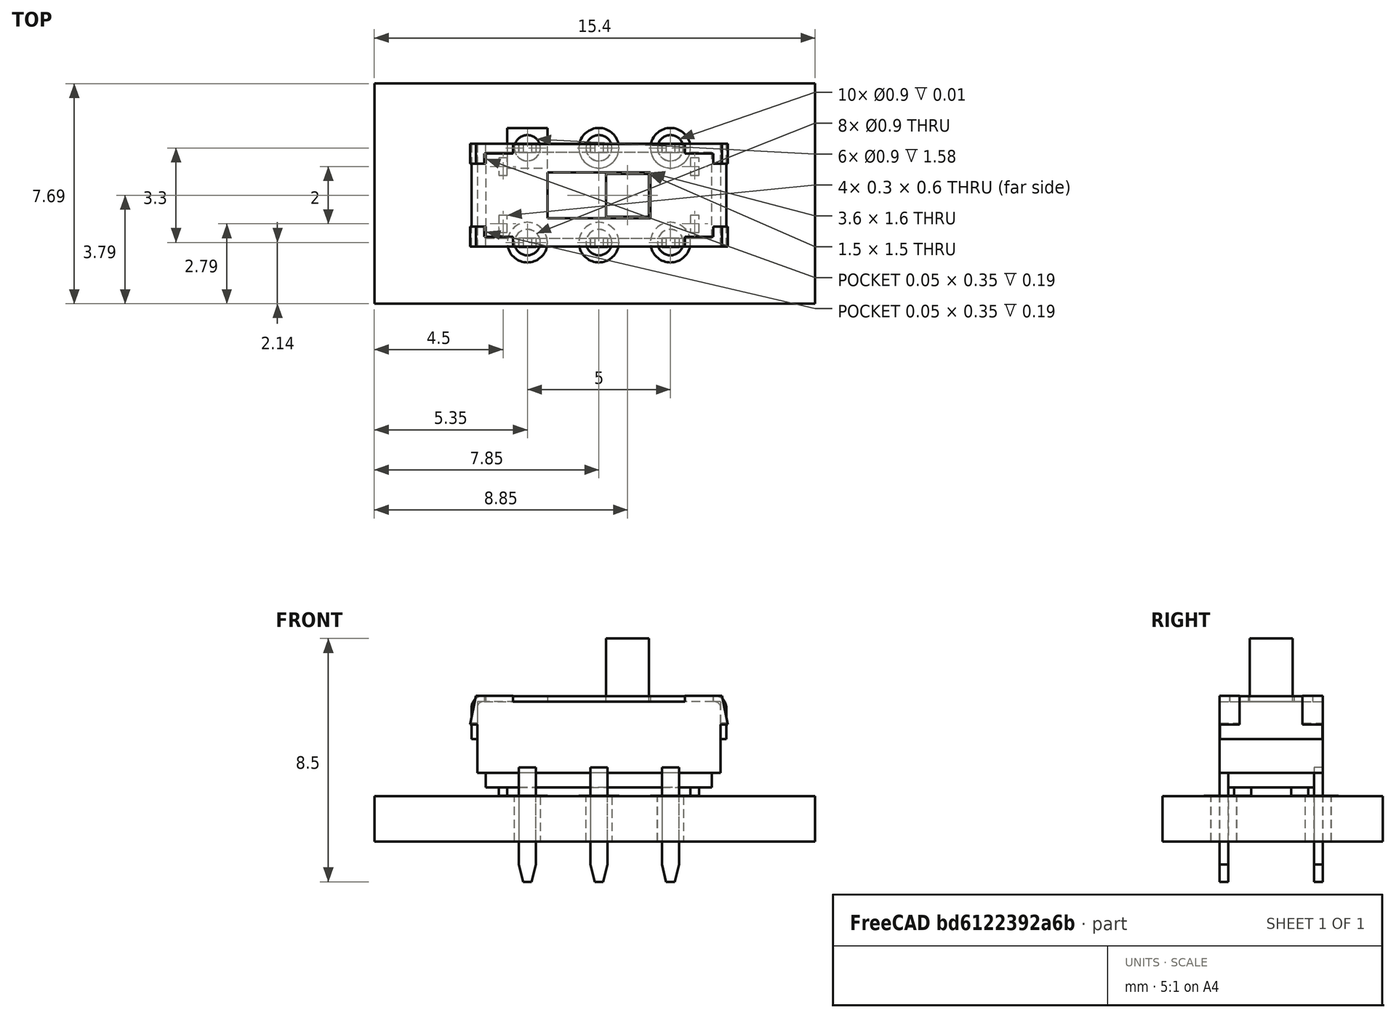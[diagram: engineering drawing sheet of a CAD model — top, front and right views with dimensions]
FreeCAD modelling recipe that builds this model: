
FCSTD DOCUMENT  (FreeCAD 0.17R10432 (Git))
Label: SW_CuK_JS202011CQN_DPDT_Straight
License: All rights reserved
LicenseURL: http://en.wikipedia.org/wiki/All_rights_reserved
objects: Sketcher::SketchObject×10, PartDesign::Pad×7, Part::FeaturePython×6, PartDesign::Pocket×3, PartDesign::Body×3, PartDesign::Plane×2, Part::MultiFuse×1, App::DocumentObjectGroup×1
note: 42 computed .brp shape members not serialized (recipe doc carries the construction recipe); baked Part::Feature solids carry a one-line shape summary decoded from their .brp

FEATURE [PartDesign::Plane] DatumPlane
  MapMode = 5
  Placement = pos=(0,0.15,0) rot=(1,0,0;1.5708rad)
  Support = -> [XZ_Plane]
  superPlacement = pos=(0,0,-0.15) rot=(0,0,1;0rad)
  expr: superPlacement.Base.z = -0.29999999999999999 / 2
FEATURE [Sketcher::SketchObject] Sketch
  MapMode = 5
  Placement = pos=(0,0.15,0) rot=(1,0,0;1.5708rad)
  Support = -> [DatumPlane]
  sketch-geometry (9):
    g0: LineSegment StartX=-1.75 StartY=0.8 StartZ=0 EndX=-1.75 EndY=2.5 EndZ=0
    g1: LineSegment StartX=-1.75 StartY=2.5 StartZ=0 EndX=-2 EndY=2.5 EndZ=0
    g2: LineSegment StartX=-2 StartY=2.5 StartZ=0 EndX=-1.8 EndY=3.5 EndZ=0
    g3: LineSegment StartX=-1.8 StartY=3.5 StartZ=0 EndX=6.8 EndY=3.5 EndZ=0
    g4: LineSegment StartX=6.8 StartY=3.5 StartZ=0 EndX=7 EndY=2.5 EndZ=0
    g5: LineSegment StartX=7 StartY=2.5 StartZ=0 EndX=6.75 EndY=2.5 EndZ=0
    g6: LineSegment StartX=6.75 StartY=2.5 StartZ=0 EndX=6.75 EndY=0.8 EndZ=0
    g7: LineSegment StartX=6.75 StartY=0.8 StartZ=0 EndX=-1.75 EndY=0.8 EndZ=0
    g8: LineSegment [constr] StartX=2.5 StartY=3.5 StartZ=0 EndX=2.5 EndY=0 EndZ=0
  constraints (26):
    c: Vertical(g0)
    c: Coincident(g0,g1)
    c: Horizontal(g1)
    c: Coincident(g1,g2)
    c: Coincident(g2,g3)
    c: Horizontal(g3)
    c: Coincident(g3,g4)
    c: Coincident(g4,g5)
    c: Horizontal(g5)
    c: Coincident(g5,g6)
    c: Vertical(g6)
    c: Coincident(g7,g0)
    c: Horizontal(g7)
    c: PointOnObject(g8,g3)
    c: Symmetric(g3,g2,g8)
    c: Symmetric(g4,g1,g8)
    c: Symmetric(g0,g6,g8)
    c: DistanceX(g-1,g8) = 2.5
    c: DistanceY(g4,g3) = 1
    c: DistanceX(g3,g4) = 0.2
    c: DistanceX(g1,g4) = 9
    c: DistanceX(g0,g6) = 8.5
    c: DistanceY(g-1,g2) = 3.5
    c: DistanceY(g-1,g0) = 0.8
    c: Coincident(g7,g6)
    c: PointOnObject(g8,g-1)
FEATURE [PartDesign::Pad] Pad
  Length = 3.6
  Length2 = 100
  Placement = pos=(0,0.15,0) rot=(1,0,0;1.5708rad)
  Profile = -> Sketch
  Type = 0
  expr: Length = 3.2999999999999998 + 0.29999999999999999
FEATURE [Sketcher::SketchObject] Sketch001
  ExternalGeometry = -> [Pad]
  MapMode = 5
  Placement = pos=(0,0.15,0.8) rot=(1,0,0;3.14159rad)
  Support = -> [Pad]
  sketch-geometry (4):
    g0: LineSegment StartX=-1.45 StartY=3.3 StartZ=0 EndX=6.45 EndY=3.3 EndZ=0
    g1: LineSegment StartX=6.45 StartY=3.3 StartZ=0 EndX=6.45 EndY=0.3 EndZ=0
    g2: LineSegment StartX=6.45 StartY=0.3 StartZ=0 EndX=-1.45 EndY=0.3 EndZ=0
    g3: LineSegment StartX=-1.45 StartY=0.3 StartZ=0 EndX=-1.45 EndY=3.3 EndZ=0
  constraints (12):
    c: Coincident(g0,g1)
    c: Coincident(g1,g2)
    c: Coincident(g2,g3)
    c: Coincident(g3,g0)
    c: Horizontal(g0)
    c: Horizontal(g2)
    c: Vertical(g1)
    c: Vertical(g3)
    c: DistanceX(g-3,g0) = 0.3
    c: DistanceY(g0,g-3) = 0.3
    c: DistanceX(g1,g-4) = 0.3
    c: DistanceY(g-4,g1) = 0.3
FEATURE [PartDesign::Pad] Pad001
  BaseFeature = -> Pad
  Length = 0.5
  Length2 = 100
  Placement = pos=(0,0.15,0) rot=(1,0,0;1.5708rad)
  Profile = -> Sketch001
  Type = 0
FEATURE [Sketcher::SketchObject] Sketch002
  ExternalGeometry = -> [Pad001]
  MapMode = 5
  Placement = pos=(0,0.15,0.3) rot=(1,0,0;3.14159rad)
  Support = -> [Pad001]
  sketch-geometry (18):
    g0: LineSegment StartX=-1 StartY=3.1 StartZ=0 EndX=-0.7 EndY=3.1 EndZ=0
    g1: LineSegment StartX=-0.7 StartY=3.1 StartZ=0 EndX=-0.7 EndY=2.5 EndZ=0
    g2: LineSegment StartX=-0.7 StartY=2.5 StartZ=0 EndX=-1 EndY=2.5 EndZ=0
    g3: LineSegment StartX=-1 StartY=2.5 StartZ=0 EndX=-1 EndY=3.1 EndZ=0
    g4: LineSegment StartX=-1 StartY=1.1 StartZ=0 EndX=-0.7 EndY=1.1 EndZ=0
    g5: LineSegment StartX=-0.7 StartY=1.1 StartZ=0 EndX=-0.7 EndY=0.5 EndZ=0
    g6: LineSegment StartX=-0.7 StartY=0.5 StartZ=0 EndX=-1 EndY=0.5 EndZ=0
    g7: LineSegment StartX=-1 StartY=0.5 StartZ=0 EndX=-1 EndY=1.1 EndZ=0
    g8: LineSegment StartX=5.7 StartY=3.1 StartZ=0 EndX=6 EndY=3.1 EndZ=0
    g9: LineSegment StartX=6 StartY=3.1 StartZ=0 EndX=6 EndY=2.5 EndZ=0
    g10: LineSegment StartX=6 StartY=2.5 StartZ=0 EndX=5.7 EndY=2.5 EndZ=0
    g11: LineSegment StartX=5.7 StartY=2.5 StartZ=0 EndX=5.7 EndY=3.1 EndZ=0
    g12: LineSegment StartX=5.7 StartY=1.1 StartZ=0 EndX=6 EndY=1.1 EndZ=0
    g13: LineSegment StartX=6 StartY=1.1 StartZ=0 EndX=6 EndY=0.5 EndZ=0
    g14: LineSegment StartX=6 StartY=0.5 StartZ=0 EndX=5.7 EndY=0.5 EndZ=0
    g15: LineSegment StartX=5.7 StartY=0.5 StartZ=0 EndX=5.7 EndY=1.1 EndZ=0
    g16: LineSegment [constr] StartX=2.5 StartY=3.3 StartZ=0 EndX=2.5 EndY=0.3 EndZ=0
    g17: LineSegment [constr] StartX=-1 StartY=1.8 StartZ=0 EndX=6 EndY=1.8 EndZ=0
  constraints (50):
    c: Coincident(g0,g1)
    c: Coincident(g1,g2)
    c: Coincident(g2,g3)
    c: Coincident(g3,g0)
    c: Horizontal(g0)
    c: Horizontal(g2)
    c: Vertical(g1)
    c: Vertical(g3)
    c: Coincident(g4,g5)
    c: Coincident(g5,g6)
    c: Coincident(g6,g7)
    c: Coincident(g7,g4)
    c: Horizontal(g4)
    c: Horizontal(g6)
    c: Vertical(g5)
    c: Vertical(g7)
    c: Coincident(g8,g9)
    c: Coincident(g9,g10)
    c: Coincident(g10,g11)
    c: Coincident(g11,g8)
    c: Horizontal(g8)
    c: Horizontal(g10)
    c: Vertical(g9)
    c: Vertical(g11)
    c: Coincident(g12,g13)
    c: Coincident(g13,g14)
    c: Coincident(g14,g15)
    c: Coincident(g15,g12)
    c: Horizontal(g12)
    c: Horizontal(g14)
    c: Vertical(g13)
    c: Vertical(g15)
    c: PointOnObject(g16,g-3)
    c: PointOnObject(g16,g-4)
    c: Vertical(g16)
    c: Horizontal(g17)
    c: Symmetric(g0,g8,g16)
    c: Symmetric(g9,g2,g16)
    c: Symmetric(g12,g4,g16)
    c: Symmetric(g5,g14,g16)
    c: Symmetric(g14,g8,g17)
    c: Symmetric(g9,g12,g17)
    c: Symmetric(g-3,g-4,g17)
    c: PointOnObject(g17,g9)
    c: Symmetric(g-3,g-3,g16)
    c: PointOnObject(g17,g3)
    c: DistanceX(g-3,g0) = 0.2
    c: DistanceY(g0,g-3) = 0.2
    c: DistanceX(g0,g0) = 0.3
    c: DistanceY(g3,g3) = 0.6
FEATURE [PartDesign::Pad] Pad002
  BaseFeature = -> Pad001
  Length = 0.3
  Length2 = 100
  Placement = pos=(0,0.15,0) rot=(1,0,0;1.5708rad)
  Profile = -> Sketch002
  Type = 0
FEATURE [Sketcher::SketchObject] Sketch003
  ExternalGeometry = -> [Pad002]
  MapMode = 5
  Placement = pos=(0,0.15,3.5) rot=(0,0,1;3.14159rad)
  Support = -> [Pad002]
  sketch-geometry (9):
    g0: LineSegment StartX=1.75 StartY=2.9 StartZ=0 EndX=2 EndY=2.9 EndZ=0
    g1: LineSegment StartX=2 StartY=2.9 StartZ=0 EndX=2 EndY=0.7 EndZ=0
    g2: LineSegment StartX=2 StartY=0.7 StartZ=0 EndX=1.75 EndY=0.7 EndZ=0
    g3: LineSegment StartX=1.75 StartY=0.7 StartZ=0 EndX=1.75 EndY=2.9 EndZ=0
    g4: LineSegment StartX=-7 StartY=2.9 StartZ=0 EndX=-6.75 EndY=2.9 EndZ=0
    g5: LineSegment StartX=-6.75 StartY=2.9 StartZ=0 EndX=-6.75 EndY=0.7 EndZ=0
    g6: LineSegment StartX=-6.75 StartY=0.7 StartZ=0 EndX=-7 EndY=0.7 EndZ=0
    g7: LineSegment StartX=-7 StartY=0.7 StartZ=0 EndX=-7 EndY=2.9 EndZ=0
    g8: LineSegment [constr] StartX=-7 StartY=1.8 StartZ=0 EndX=2 EndY=1.8 EndZ=0
  constraints (26):
    c: Coincident(g0,g1)
    c: Coincident(g1,g2)
    c: Coincident(g2,g3)
    c: Coincident(g3,g0)
    c: Horizontal(g0)
    c: Horizontal(g2)
    c: Vertical(g1)
    c: Vertical(g3)
    c: PointOnObject(g1,g-8)
    c: Coincident(g4,g5)
    c: Coincident(g5,g6)
    c: Coincident(g6,g7)
    c: Coincident(g7,g4)
    c: Horizontal(g4)
    c: Horizontal(g6)
    c: Vertical(g5)
    c: Vertical(g7)
    c: PointOnObject(g4,g-7)
    c: PointOnObject(g8,g-7)
    c: PointOnObject(g8,g-8)
    c: Symmetric(g-8,g-8,g8)
    c: Symmetric(g1,g0,g8)
    c: DistanceY(g0,g-8) = 0.7
    c: Symmetric(g4,g5,g8)
    c: PointOnObject(g5,g-6)
    c: PointOnObject(g2,g-5)
FEATURE [PartDesign::Pocket] Pocket
  BaseFeature = -> Pad002
  Length = 5
  Placement = pos=(0,0.15,0) rot=(1,0,0;1.5708rad)
  Profile = -> Sketch003
  Type = 1
FEATURE [Sketcher::SketchObject] Sketch004
  ExternalGeometry = -> [Pocket]
  MapMode = 5
  Placement = pos=(0,0.15,3.5) rot=(0,0,1;3.14159rad)
  Support = -> [Pocket]
  sketch-geometry (22):
    g0: LineSegment [constr] StartX=-6.75 StartY=1.8 StartZ=0 EndX=1.75 EndY=1.8 EndZ=0
    g1: LineSegment [constr] StartX=-2.5 StartY=3.25 StartZ=0 EndX=-2.5 EndY=0.35 EndZ=0
    g2: LineSegment StartX=-5.5 StartY=3.6 StartZ=0 EndX=-5.5 EndY=3.25 EndZ=0
    g3: LineSegment StartX=-5.5 StartY=3.25 StartZ=0 EndX=-6.5 EndY=3.25 EndZ=0
    g4: LineSegment StartX=-6.5 StartY=0.35 StartZ=0 EndX=-5.5 EndY=0.35 EndZ=0
    g5: LineSegment StartX=-5.5 StartY=0.35 StartZ=0 EndX=-5.5 EndY=0 EndZ=0
    g6: LineSegment StartX=-5.5 StartY=0 StartZ=0 EndX=0.5 EndY=0 EndZ=0
    g7: LineSegment StartX=0.5 StartY=0 StartZ=0 EndX=0.5 EndY=0.35 EndZ=0
    g8: LineSegment StartX=0.5 StartY=0.35 StartZ=0 EndX=1.5 EndY=0.35 EndZ=0
    g9: LineSegment StartX=1.5 StartY=3.25 StartZ=0 EndX=0.5 EndY=3.25 EndZ=0
    g10: LineSegment StartX=0.5 StartY=3.25 StartZ=0 EndX=0.5 EndY=3.6 EndZ=0
    g11: LineSegment StartX=0.5 StartY=3.6 StartZ=0 EndX=-5.5 EndY=3.6 EndZ=0
    g12: LineSegment StartX=-6.5 StartY=3.25 StartZ=0 EndX=-6.5 EndY=2.9 EndZ=0
    g13: LineSegment StartX=-6.5 StartY=2.9 StartZ=0 EndX=-6.75 EndY=2.9 EndZ=0
    g14: LineSegment StartX=-6.75 StartY=2.9 StartZ=0 EndX=-6.75 EndY=0.7 EndZ=0
    g15: LineSegment StartX=-6.75 StartY=0.7 StartZ=0 EndX=-6.5 EndY=0.7 EndZ=0
    g16: LineSegment StartX=-6.5 StartY=0.7 StartZ=0 EndX=-6.5 EndY=0.35 EndZ=0
    g17: LineSegment StartX=1.5 StartY=3.25 StartZ=0 EndX=1.5 EndY=2.9 EndZ=0
    g18: LineSegment StartX=1.5 StartY=2.9 StartZ=0 EndX=1.75 EndY=2.9 EndZ=0
    g19: LineSegment StartX=1.75 StartY=2.9 StartZ=0 EndX=1.75 EndY=0.7 EndZ=0
    g20: LineSegment StartX=1.75 StartY=0.7 StartZ=0 EndX=1.5 EndY=0.7 EndZ=0
    g21: LineSegment StartX=1.5 StartY=0.7 StartZ=0 EndX=1.5 EndY=0.35 EndZ=0
  constraints (60):
    c: Horizontal(g0)
    c: Vertical(g2)
    c: Coincident(g2,g3)
    c: Horizontal(g3)
    c: Horizontal(g4)
    c: Coincident(g4,g5)
    c: Vertical(g5)
    c: Coincident(g5,g6)
    c: Coincident(g6,g7)
    c: Vertical(g7)
    c: Coincident(g7,g8)
    c: Horizontal(g8)
    c: Horizontal(g9)
    c: Coincident(g9,g10)
    c: Coincident(g10,g11)
    c: Vertical(g10)
    c: Symmetric(g2,g4,g0)
    c: Symmetric(g9,g2,g1)
    c: Symmetric(g4,g7,g1)
    c: DistanceY(g5,g5) = 0.35
    c: DistanceX(g4,g4) = 1
    c: Coincident(g11,g2)
    c: PointOnObject(g6,g-7)
    c: PointOnObject(g5,g-7)
    c: PointOnObject(g2,g-5)
    c: PointOnObject(g10,g-5)
    c: PointOnObject(g1,g9)
    c: PointOnObject(g1,g8)
    c: Symmetric(g-5,g-5,g1)
    c: Symmetric(g-7,g-5,g0)
    c: Coincident(g3,g12)
    c: Vertical(g12)
    c: Coincident(g12,g13)
    c: Coincident(g13,g-4)
    c: Coincident(g13,g14)
    c: Coincident(g14,g-4)
    c: Coincident(g14,g15)
    c: Horizontal(g15)
    c: Coincident(g15,g16)
    c: Coincident(g16,g4)
    c: Vertical(g16)
    c: Horizontal(g13)
    c: Coincident(g9,g17)
    c: Vertical(g17)
    c: Coincident(g17,g18)
    c: Coincident(g18,g-6)
    c: Horizontal(g18)
    c: Coincident(g18,g19)
    c: Coincident(g19,g-6)
    c: Coincident(g19,g20)
    c: Horizontal(g20)
    c: Coincident(g20,g21)
    c: Coincident(g21,g8)
    c: Vertical(g21)
    c: DistanceX(g13,g13) = 0.25
    c: Symmetric(g17,g12,g1)
    c: Symmetric(g20,g15,g1)
    c: PointOnObject(g12,g16)
    c: PointOnObject(g0,g-4)
    c: PointOnObject(g0,g-6)
FEATURE [PartDesign::Pocket] Pocket001
  BaseFeature = -> Pocket
  Length = 0.2
  Placement = pos=(0,0.15,0) rot=(1,0,0;1.5708rad)
  Profile = -> Sketch004
  Type = 0
FEATURE [PartDesign::Plane] DatumPlane001
  MapMode = 5
  Placement = pos=(0,-0.55,0) rot=(1,0,0;1.5708rad)
  Support = -> [XZ_Plane001]
  superPlacement = pos=(0,0,0.55) rot=(0,0,1;0rad)
  expr: superPlacement.Base.z = -0.29999999999999999 / 2 + 0.69999999999999996
FEATURE [Sketcher::SketchObject] Sketch007
  MapMode = 5
  Placement = pos=(0,-0.55,0) rot=(1,0,0;1.5708rad)
  Support = -> [DatumPlane001]
  sketch-geometry (13):
    g0: LineSegment StartX=-1.95 StartY=1.99 StartZ=0 EndX=-1.95 EndY=3.09 EndZ=0
    g1: LineSegment StartX=-1.55 StartY=3.49 StartZ=0 EndX=6.55 EndY=3.49 EndZ=0
    g2: LineSegment StartX=6.95 StartY=3.09 StartZ=0 EndX=6.95 EndY=1.99 EndZ=0
    g3: LineSegment StartX=6.95 StartY=1.99 StartZ=0 EndX=6.75 EndY=1.99 EndZ=0
    g4: LineSegment StartX=6.75 StartY=1.99 StartZ=0 EndX=6.75 EndY=3.09 EndZ=0
    g5: LineSegment StartX=6.55 StartY=3.29 StartZ=0 EndX=-1.55 EndY=3.29 EndZ=0
    g6: LineSegment StartX=-1.75 StartY=3.09 StartZ=0 EndX=-1.75 EndY=1.99 EndZ=0
    g7: LineSegment StartX=-1.75 StartY=1.99 StartZ=0 EndX=-1.95 EndY=1.99 EndZ=0
    g8: ArcOfCircle CenterX=-1.55 CenterY=3.09 CenterZ=0 NormalX=0 NormalY=0 NormalZ=1 Radius=0.2 StartAngle=1.5708 EndAngle=3.14159
    g9: ArcOfCircle CenterX=-1.55 CenterY=3.09 CenterZ=0 NormalX=0 NormalY=0 NormalZ=1 Radius=0.4 StartAngle=1.5708 EndAngle=3.14159
    g10: ArcOfCircle CenterX=6.55 CenterY=3.09 CenterZ=0 NormalX=0 NormalY=0 NormalZ=1 Radius=0.4 StartAngle=0 EndAngle=1.5708
    g11: ArcOfCircle CenterX=6.55 CenterY=3.09 CenterZ=0 NormalX=0 NormalY=0 NormalZ=1 Radius=0.2 StartAngle=0 EndAngle=1.5708
    g12: LineSegment [constr] StartX=2.5 StartY=3.49 StartZ=0 EndX=2.5 EndY=0 EndZ=0
  constraints (33):
    c: Vertical(g0)
    c: Horizontal(g1)
    c: Vertical(g2)
    c: Coincident(g2,g3)
    c: Horizontal(g3)
    c: Coincident(g3,g4)
    c: Horizontal(g5)
    c: Vertical(g6)
    c: Coincident(g6,g7)
    c: Coincident(g7,g0)
    c: Horizontal(g7)
    c: Tangent(g6,g8) = -1.5708
    c: Tangent(g5,g8) = -1.5708
    c: Tangent(g0,g9) = 1.5708
    c: Tangent(g1,g9) = 1.5708
    c: Tangent(g1,g10) = 1.5708
    c: Tangent(g2,g10) = 1.5708
    c: Tangent(g5,g11) = -1.5708
    c: Tangent(g4,g11) = -1.5708
    c: Vertical(g4)
    c: Coincident(g10,g11)
    c: Coincident(g8,g9)
    c: PointOnObject(g12,g1)
    c: PointOnObject(g12,g-1)
    c: Vertical(g12)
    c: DistanceX(g-1,g12) = 2.5
    c: Symmetric(g2,g0,g12)
    c: Equal(g8,g11)
    c: DistanceY(g5,g1) = 0.2
    c: DistanceY(g-1,g1) = 3.49
    c: Radius(g8) = 0.2
    c: DistanceX(g0,g2) = 8.9
    c: DistanceY(g6,g1) = 1.5
FEATURE [PartDesign::Pad] Pad004
  Length = 2.2
  Length2 = 100
  Placement = pos=(0,-0.55,0) rot=(1,0,0;1.5708rad)
  Profile = -> Sketch007
  Type = 0
  expr: Length = 3.2999999999999998 + 0.29999999999999999 - 2 * 0.69999999999999996
FEATURE [Sketcher::SketchObject] Sketch008
  ExternalGeometry = -> [Pad004]
  MapMode = 5
  Placement = pos=(0,-0.55,0) rot=(-1,0,0;1.5708rad)
  Support = -> [Pad004]
  sketch-geometry (12):
    g0: LineSegment StartX=-1.45 StartY=-3.29 StartZ=0 EndX=6.5 EndY=-3.29 EndZ=0
    g1: LineSegment StartX=6.5 StartY=-3.29 StartZ=0 EndX=6.5 EndY=-3.49 EndZ=0
    g2: LineSegment StartX=6.5 StartY=-3.49 StartZ=0 EndX=-1.45 EndY=-3.49 EndZ=0
    g3: LineSegment StartX=-1.45 StartY=-3.49 StartZ=0 EndX=-1.45 EndY=-3.29 EndZ=0
    g4: LineSegment StartX=6.75 StartY=-1.99 StartZ=0 EndX=6.95 EndY=-1.99 EndZ=0
    g5: LineSegment StartX=6.95 StartY=-1.99 StartZ=0 EndX=6.95 EndY=-2.54 EndZ=0
    g6: LineSegment StartX=6.95 StartY=-2.54 StartZ=0 EndX=6.75 EndY=-2.54 EndZ=0
    g7: LineSegment StartX=6.75 StartY=-2.54 StartZ=0 EndX=6.75 EndY=-1.99 EndZ=0
    g8: LineSegment StartX=-1.95 StartY=-1.99 StartZ=0 EndX=-1.75 EndY=-1.99 EndZ=0
    g9: LineSegment StartX=-1.75 StartY=-1.99 StartZ=0 EndX=-1.75 EndY=-2.54 EndZ=0
    g10: LineSegment StartX=-1.75 StartY=-2.54 StartZ=0 EndX=-1.95 EndY=-2.54 EndZ=0
    g11: LineSegment StartX=-1.95 StartY=-2.54 StartZ=0 EndX=-1.95 EndY=-1.99 EndZ=0
  constraints (34):
    c: Coincident(g0,g1)
    c: Coincident(g1,g2)
    c: Coincident(g2,g3)
    c: Coincident(g3,g0)
    c: Horizontal(g0)
    c: Horizontal(g2)
    c: Vertical(g1)
    c: Vertical(g3)
    c: PointOnObject(g0,g-4)
    c: PointOnObject(g1,g-3)
    c: Coincident(g4,g5)
    c: Coincident(g5,g6)
    c: Coincident(g6,g7)
    c: Coincident(g7,g4)
    c: Horizontal(g4)
    c: Horizontal(g6)
    c: Vertical(g5)
    c: Vertical(g7)
    c: Coincident(g4,g-7)
    c: PointOnObject(g5,g-8)
    c: Coincident(g8,g9)
    c: Coincident(g9,g10)
    c: Coincident(g10,g11)
    c: Coincident(g11,g8)
    c: Horizontal(g8)
    c: Horizontal(g10)
    c: Vertical(g9)
    c: Vertical(g11)
    c: Coincident(g8,g-6)
    c: PointOnObject(g9,g-5)
    c: DistanceY(g9,g8) = 0.55
    c: PointOnObject(g9,g6)
    c: DistanceX(g-4,g0) = 0.1
    c: DistanceX(g0,g-4) = 0.05
FEATURE [PartDesign::Pad] Pad005
  BaseFeature = -> Pad004
  Length = 0.69
  Length2 = 2.89
  Placement = pos=(0,-0.55,0) rot=(1,0,0;1.5708rad)
  Profile = -> Sketch008
  Type = 4
  expr: Length2 = 3.2999999999999998 + 0.29999999999999999 - 0.69999999999999996 - 0.01
FEATURE [Sketcher::SketchObject] Sketch011
  ExternalGeometry = -> [Pad005]
  MapMode = 5
  Placement = pos=(0,-0.55,3.49) rot=(0,0,1;3.14159rad)
  Support = -> [Pad005]
  sketch-geometry (6):
    g0: LineSegment StartX=-4.3 StartY=1.9 StartZ=0 EndX=-0.7 EndY=1.9 EndZ=0
    g1: LineSegment StartX=-0.7 StartY=1.9 StartZ=0 EndX=-0.7 EndY=0.3 EndZ=0
    g2: LineSegment StartX=-0.7 StartY=0.3 StartZ=0 EndX=-4.3 EndY=0.3 EndZ=0
    g3: LineSegment StartX=-4.3 StartY=0.3 StartZ=0 EndX=-4.3 EndY=1.9 EndZ=0
    g4: LineSegment [constr] StartX=-4.3 StartY=1.1 StartZ=0 EndX=-0.7 EndY=1.1 EndZ=0
    g5: LineSegment [constr] StartX=-2.5 StartY=1.9 StartZ=0 EndX=-2.5 EndY=0.3 EndZ=0
  constraints (19):
    c: Coincident(g0,g1)
    c: Coincident(g1,g2)
    c: Coincident(g2,g3)
    c: Coincident(g3,g0)
    c: Horizontal(g0)
    c: Horizontal(g2)
    c: Vertical(g1)
    c: Vertical(g3)
    c: PointOnObject(g4,g3)
    c: PointOnObject(g4,g1)
    c: PointOnObject(g5,g0)
    c: PointOnObject(g5,g2)
    c: Vertical(g5)
    c: Symmetric(g0,g0,g5)
    c: Symmetric(g1,g0,g4)
    c: Symmetric(g-3,g-4,g4)
    c: Symmetric(g-3,g-3,g5)
    c: DistanceX(g0,g0) = 3.6
    c: DistanceY(g1,g1) = 1.6
FEATURE [PartDesign::Pocket] Pocket003
  BaseFeature = -> Pad005
  Length = 5
  Placement = pos=(0,-0.55,0) rot=(1,0,0;1.5708rad)
  Profile = -> Sketch011
  Type = 2
FEATURE [PartDesign::Body] Body001  label="TopMetal"
  Origin = -> Body001Origin
  Tip = -> Pocket003
FEATURE [Sketcher::SketchObject] Sketch012
  ExternalGeometry = -> [Pocket001]
  MapMode = 5
  Placement = pos=(0,0.15,3.3) rot=(0,0,1;3.14159rad)
  Support = -> [Pocket001]
  sketch-geometry (7):
    g0: LineSegment [constr] StartX=-2.5 StartY=3.6 StartZ=0 EndX=-2.5 EndY=0 EndZ=0
    g1: LineSegment [constr] StartX=-3.5 StartY=1.8 StartZ=0 EndX=-1.5 EndY=1.8 EndZ=0
    g2: LineSegment StartX=-4.25 StartY=2.55 StartZ=0 EndX=-2.75 EndY=2.55 EndZ=0
    g3: LineSegment StartX=-2.75 StartY=2.55 StartZ=0 EndX=-2.75 EndY=1.05 EndZ=0
    g4: LineSegment StartX=-2.75 StartY=1.05 StartZ=0 EndX=-4.25 EndY=1.05 EndZ=0
    g5: LineSegment StartX=-4.25 StartY=1.05 StartZ=0 EndX=-4.25 EndY=2.55 EndZ=0
    g6: LineSegment [constr] StartX=-3.5 StartY=2.55 StartZ=0 EndX=-3.5 EndY=1.05 EndZ=0
  constraints (24):
    c: PointOnObject(g0,g-3)
    c: PointOnObject(g0,g-4)
    c: Vertical(g0)
    c: Symmetric(g-3,g-3,g0)
    c: Horizontal(g1)
    c: DistanceX(g1,g1) = 2
    c: Symmetric(g0,g0,g1)
    c: Symmetric(g1,g1,g0)
    c: Coincident(g2,g3)
    c: Coincident(g3,g4)
    c: Coincident(g4,g5)
    c: Coincident(g5,g2)
    c: Horizontal(g2)
    c: Horizontal(g4)
    c: Vertical(g3)
    c: Vertical(g5)
    c: PointOnObject(g6,g2)
    c: PointOnObject(g6,g4)
    c: Vertical(g6)
    c: PointOnObject(g1,g6)
    c: Symmetric(g2,g2,g6)
    c: Symmetric(g2,g3,g1)
    c: DistanceX(g2,g2) = 1.5
    c: DistanceY(g5,g5) = 1.5
FEATURE [PartDesign::Pad] Pad006
  BaseFeature = -> Pocket001
  Length = 2.2
  Length2 = 100
  Placement = pos=(0,0.15,0) rot=(1,0,0;1.5708rad)
  Profile = -> Sketch012
  Type = 0
FEATURE [PartDesign::Body] Body  label="MainBody"
  Origin = -> BodyOrigin
  Tip = -> Pad006
FEATURE [Sketcher::SketchObject] Sketch013
  MapMode = 5
  Placement = pos=(0,0,0) rot=(1,0,0;1.5708rad)
  Support = -> [XZ_Plane002]
  sketch-geometry (7):
    g0: GeomPoint [constr] X=0 Y=3.5 Z=0
    g1: LineSegment StartX=-0.3 StartY=1 StartZ=0 EndX=-0.3 EndY=-2.4 EndZ=0
    g2: LineSegment StartX=-0.3 StartY=-2.4 StartZ=0 EndX=-0.15 EndY=-3 EndZ=0
    g3: LineSegment StartX=-0.15 StartY=-3 StartZ=0 EndX=0.15 EndY=-3 EndZ=0
    g4: LineSegment StartX=0.15 StartY=-3 StartZ=0 EndX=0.3 EndY=-2.4 EndZ=0
    g5: LineSegment StartX=0.3 StartY=-2.4 StartZ=0 EndX=0.3 EndY=1 EndZ=0
    g6: LineSegment StartX=0.3 StartY=1 StartZ=0 EndX=-0.3 EndY=1 EndZ=0
  constraints (19):
    c: PointOnObject(g0,g-2)
    c: DistanceY(g-1,g0) = 3.5
    c: Vertical(g1)
    c: Coincident(g1,g2)
    c: Coincident(g2,g3)
    c: Horizontal(g3)
    c: Coincident(g3,g4)
    c: Coincident(g4,g5)
    c: Vertical(g5)
    c: Coincident(g5,g6)
    c: Coincident(g6,g1)
    c: Horizontal(g6)
    c: Symmetric(g4,g1,g-2)
    c: Symmetric(g3,g2,g-2)
    c: DistanceY(g4,g4) = 0.6
    c: DistanceX(g6,g6) = 0.6
    c: DistanceX(g3,g4) = 0.15
    c: DistanceY(g-1,g5) = 1
    c: DistanceY(g2,g0) = 6.5
FEATURE [PartDesign::Pad] Pad007
  Length = 0.31
  Length2 = 100
  Midplane = true
  Placement = pos=(0,0,0) rot=(1,0,0;1.5708rad)
  Profile = -> Sketch013
  Type = 0
FEATURE [PartDesign::Body] Body002  label="Pin"
  Origin = -> Body002Origin
  Tip = -> Pad007
FEATURE [Part::FeaturePython] Array  # Draft array (typed FeaturePython)
  Angle = 360
  ArrayType = 0
  Axis = (0,0,1)
  Base = -> Pad007
  Center = (0,0,0)
  Fuse = false
  IntervalAxis = (0,0,0)
  IntervalX = (2.5,0,0)
  IntervalY = (0,-3.3,0)
  IntervalZ = (0,0,0)
  NumberPolar = 1
  NumberX = 3
  NumberY = 2
  NumberZ = 1
FEATURE [Part::MultiFuse] Fusion  label="SW_CuK_JS202011CQN_DPDT_Straight"
  Shapes = -> [Array,Pocket003,Pad006]
FEATURE [Part::FeaturePython] Filk_lines  label="FrontSilk"  # a2plus imported part (geometry in sourceFile) (typed FeaturePython)
  fixedPosition = true
FEATURE [Part::FeaturePython] TopPads  # a2plus imported part (geometry in sourceFile) (typed FeaturePython)
  fixedPosition = true
FEATURE [Part::FeaturePython] BotPads  # a2plus imported part (geometry in sourceFile) (typed FeaturePython)
  fixedPosition = true
FEATURE [Part::FeaturePython] THPs  label="PTHs"  # a2plus imported part (geometry in sourceFile) (typed FeaturePython)
  fixedPosition = true
FEATURE [Part::FeaturePython] newPCB  label="Pcb"  # a2plus imported part (geometry in sourceFile) (typed FeaturePython)
  fixedPosition = true
FEATURE [App::DocumentObjectGroup] SW_CuK_JS202011CQN_DPDT_Straight_fp
  Group = -> [Filk_lines,TopPads,BotPads,THPs,newPCB]
